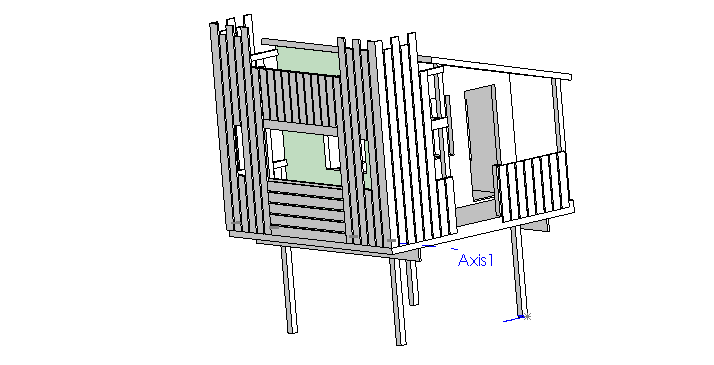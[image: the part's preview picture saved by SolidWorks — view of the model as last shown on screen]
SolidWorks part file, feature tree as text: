
SOLIDWORKS PART (.sldprt)
format: sldprt  version: not decoded by parser v0  size: 1,766,912 bytes
history: native  units: mm
features: sketch x28, extrude x20, cut_extrude x8, plane x3, shell x1 (+11 scaffold rows collapsed)
feature tree (71):
  scaffold x11  (default folders/planes/origin — collapsed)
  sketch  "Sketch1"  dims[c1.D1=101.6mm c1.D2=101.6mm c2.D1=101.6mm c2.D2=101.6mm c2.D3=90.0deg c2.D4=3048.0mm]
  extrude  "Extrude1"  Depth=1524mm
  sketch  "Sketch2"  dims[D1=38.1mm D2=38.1mm D3=3657.6mm D4=609.6mm]
  extrude  "Extrude2"  Depth=190.5mm
  plane  "Plane1"  Offset=2.54mm
  sketch  "Sketch3"  dims[D1=3657.6mm D2=3657.6mm D3=520.7mm D4=3657.6mm]
  extrude  "Extrude3"  Depth=190.5mm
  plane  "Floor"  Offset=2.54mm
  sketch  "Sketch4"  dims[D1=2438.4mm D2=2438.4mm]
  extrude  "Extrude4"  Depth=1828.8mm
  sketch  "Sketch5"  dims[D1=660.4mm]
  extrude  "Extrude5"  [1 undecoded]
  shell  "Shell1"  Thickness=88.9mm
  sketch  "Sketch6"  dims[D1=152.4mm D2=152.4mm D3=152.4mm]
  extrude  "Extrude6"  Depth=88.9mm
  sketch  "Sketch7"  dims[c1.D1=88.9mm c1.D2=38.1mm c1.D3=38.1mm c1.D4=38.1mm c1.D5=38.1mm c1.D6=38.1mm c1.D7=38.1mm c1.D8=38.1mm c1.D9=1219.2mm c2.D6=762.0mm c2.D7=762.0mm]
  extrude  "Extrude7"  Depth=2438.4mm
  sketch  "Sketch8"  dims[c1.D1=88.9mm c1.D2=38.1mm c1.D3=38.1mm c2.D2=1219.2mm]
  extrude  "Extrude8"  [1 undecoded]
  sketch  "Sketch9"  dims[D1=88.9mm D2=914.4mm]
  extrude  "Extrude9"  Depth=762mm
  sketch  "Sketch10"  dims[D1=609.6mm D2=38.1mm D3=304.8mm D4=1676.4mm D5=304.8mm D6=914.4mm]
  cut_extrude  "Cut-Extrude1"  [1 undecoded]
  sketch  "Sketch11"  dims[D1=139.7mm D2=1524.0mm]
  extrude  "Extrude10"  Depth=38.1mm
  sketch  "Sketch12"  dims[D1=914.4mm D2=762.0mm D3=457.2mm]
  cut_extrude  "Cut-Extrude2"  Depth=127mm
  sketch  "Sketch13"  dims[D1=914.4mm D2=685.8mm D3=609.6mm]
  cut_extrude  "Cut-Extrude3"  Depth=127mm
  sketch  "Sketch14"  dims[D1=914.4mm D2=457.2mm D3=609.6mm]
  cut_extrude  "Cut-Extrude4"  Depth=127mm
  sketch  "Sketch15"  dims[D1=88.9mm]
  extrude  "Extrude11"  Depth=38.1mm
  sketch  "Sketch16"
  extrude  "Extrude12"  Depth=38.1mm
  sketch  "Sketch17"  dims[D1=88.9mm D2=88.9mm D3=762.0mm]
  extrude  "Extrude13"  Depth=38.1mm
  sketch  "Sketch18"  dims[D1=38.1mm D2=609.6mm]
  extrude  "Extrude14"  [1 undecoded]
  sketch  "Sketch19"
  extrude  "Extrude15"  Depth=38.1mm
  sketch  "Sketch20"
  extrude  "Extrude16"  Depth=38.1mm
  sketch  "Sketch21"  dims[D1=142.875mm D2=25.4mm D3=25.4mm D4=25.4mm D5=25.4mm D6=25.4mm D7=25.4mm D8=142.875mm D9=25.4mm D10=25.4mm D11=25.4mm D12=25.4mm D13=25.4mm D14=25.4mm D15=25.4mm D16=25.4mm D17=25.4mm D18=25.4mm D19=142.875mm D20=25.4mm D21=25.4mm D22=25.4mm D23=25.4mm D24=25.4mm D25=25.4mm D26=142.875mm D27=142.875mm]
  extrude  "Extrude18"  Depth=3048mm
  plane  "PorchFloor"  Offset=2.54mm
  sketch  "Sketch22"  dims[D1=25.4mm D2=142.875mm]
  extrude  "Extrude19"  [1 undecoded]
  sketch  "Sketch23"  dims[c1.D1=142.875mm c1.D2=25.4mm c1.D3=25.4mm c1.D4=25.4mm c1.D5=142.875mm c1.D6=142.875mm c1.D7=25.4mm c1.D8=142.875mm c1.D9=142.875mm c1.D10=25.4mm c2.D2=31.75mm]
  extrude  "Extrude20"  Depth=88.9mm
  sketch  "Sketch24"  dims[D1=152.4mm D2=152.4mm]
  cut_extrude  "Cut-Extrude5"  Depth=50.8mm
  sketch  "Sketch25"  dims[D1=152.4mm]
  cut_extrude  "Cut-Extrude6"  Depth=50.8mm
  sketch  "Sketch26"  dims[D1=152.4mm]
  cut_extrude  "Cut-Extrude7"  Depth=50.8mm
  sketch  "Sketch27"  dims[D1=171.45mm D2=508.0mm D3=508.0mm]
  cut_extrude  "Cut-Extrude9"  Depth=50.8mm
  sketch  "Sketch28"  dims[D1=142.875mm D2=88.9mm D3=25.4mm]
  extrude  "Extrude21"  [1 undecoded]
decode coverage: 48 of 57 modeling features carry decoded parameters
note: 6 parameter values undecoded
summary: no parameter record found for 6 features
note: suppression state not decoded; provenance and decode notes live in map.json
